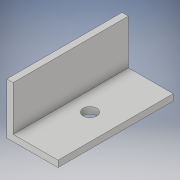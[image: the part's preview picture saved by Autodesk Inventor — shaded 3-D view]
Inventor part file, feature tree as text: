
AUTODESK INVENTOR PART (.ipt)
format: ipt  version: 2017 (Build 210142000, 142)  size: 109,568 bytes
history: native  units: in
note: dims shown in document units (in); Inventor stores cm internally (conversion verified against a paired STEP export)
features: sketch x2, extrude x1, hole x1
ambient origin geometry x8: Origin, YZ Plane, XZ Plane, XY Plane, X Axis, Y Axis, Z Axis, Center Point
bodies: Solid1 (feature_tree)
feature tree (4):
  extrude  "Extrusion1"  Depth=1.0in
  hole  "Hole1"  [1 undecoded]
  sketch  "Sketch1"  dims[d4=2.25in d5=0.0in d6=1.0in]
  sketch  "Sketch2"  dims[d7=1.0in d8=0.5in d9=1.125in d10=1.125in d11=0.266in d12=0.75in d13=0.507in d14=0.25in d15=0.5635in d16=1.0in d17=0.8108in]
note: 1 required parameter value undecoded (feature->parameter linkage not recoverable at this tier; creation-order binding heuristic only, values carry confidence <= 0.55)
